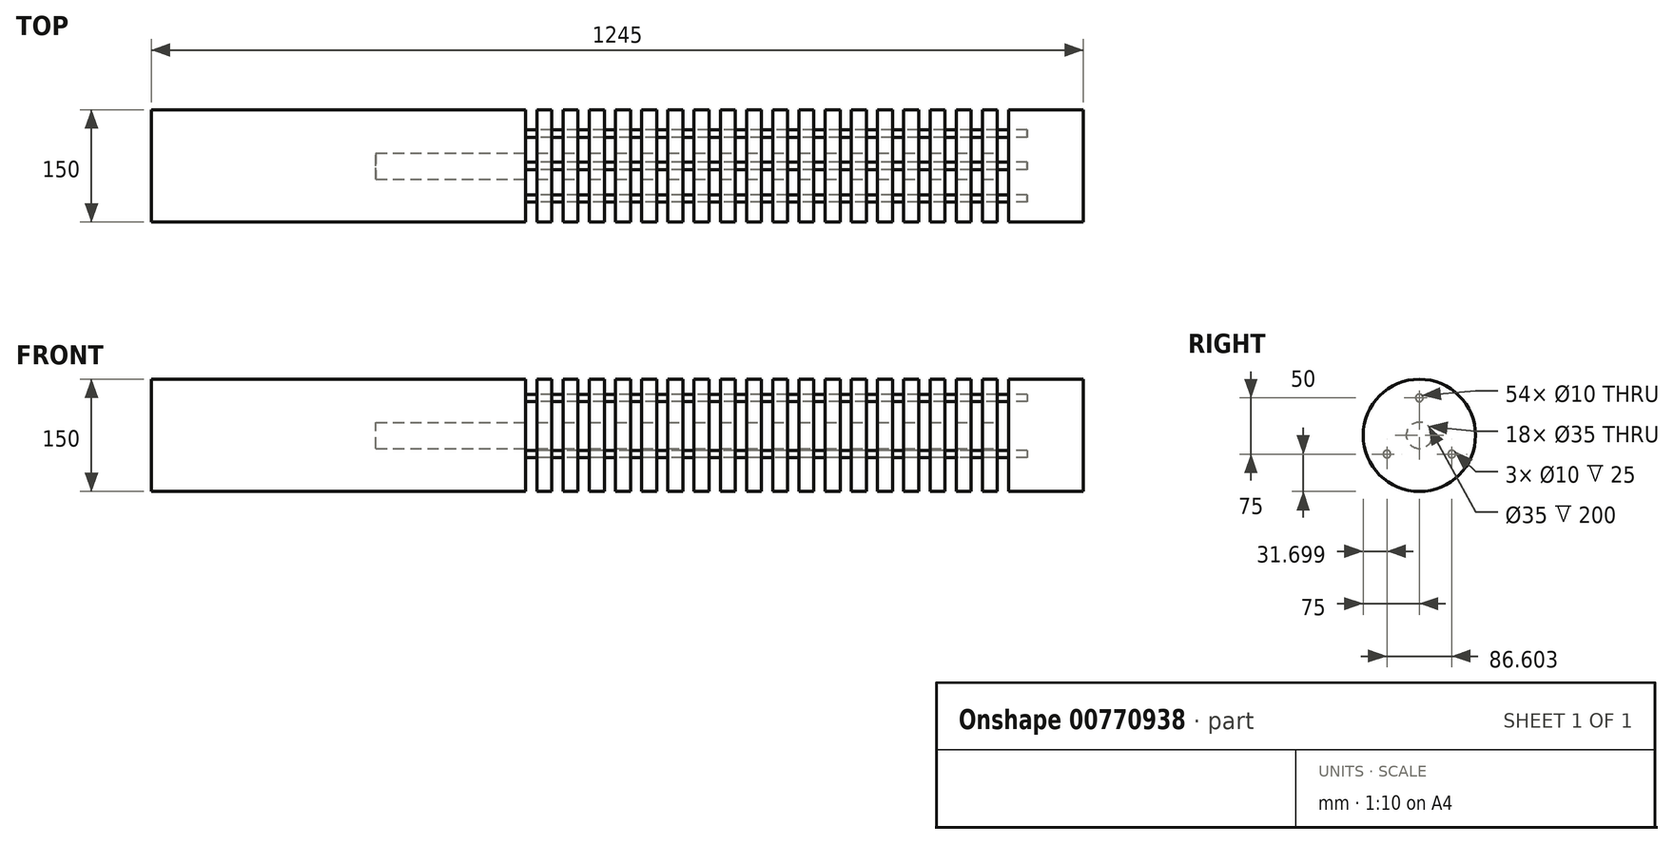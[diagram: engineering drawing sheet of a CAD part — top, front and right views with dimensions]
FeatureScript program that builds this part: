
annotation { "Feature Type Name" : "Feature", "Feature Type Description" : "" }
export const myFeature = defineFeature(function(context is Context, id is Id, definition is map)
    precondition{}
    {
        {
            var Q0;
            Q0=qCreatedBy(makeId("Top.planeOp"),FACE);
            var sketch = newSketch(context, id + "F0", { "sketchPlane" : qUnion([Q0])});
            skLineSegment(sketch, "E0", {"start": v(-500, 0) * mm, "end": v(-500, -75) * mm});
            skLineSegment(sketch, "E1", {"start": v(-500, -75) * mm, "end": v(0, -75) * mm});
            skLineSegment(sketch, "E2", {"start": v(0, -75) * mm, "end": v(0, -17.5) * mm});
            skLineSegment(sketch, "E3", {"start": v(0, -17.5) * mm, "end": v(-200, -17.5) * mm});
            skLineSegment(sketch, "E4", {"start": v(-200, -17.5) * mm, "end": v(-200, 0) * mm});
            skLineSegment(sketch, "E5", {"start": v(-200, 0) * mm, "end": v(-500, 0) * mm});
            skSolve(sketch);
        }
        {
            var Q0;
            Q0=qCreatedBy(makeId("Top.planeOp"),FACE);
            var sketch = newSketch(context, id + "F1", { "sketchPlane" : qUnion([Q0])});
            skLineSegment(sketch, "E6.bottom", {"start": v(15, -17.5) * mm, "end": v(35, -17.5) * mm});
            skLineSegment(sketch, "E6.top", {"start": v(15, -75) * mm, "end": v(35, -75) * mm});
            skLineSegment(sketch, "E6.left", {"start": v(15, -17.5) * mm, "end": v(15, -75) * mm});
            skLineSegment(sketch, "E6.right", {"start": v(35, -17.5) * mm, "end": v(35, -75) * mm});
            skLineSegment(sketch, "E7.1.0.0", {"start": v(50, -75) * mm, "end": v(70, -75) * mm});
            skLineSegment(sketch, "E7.1.0.1", {"start": v(70, -17.5) * mm, "end": v(70, -75) * mm});
            skLineSegment(sketch, "E7.1.0.2", {"start": v(50, -17.5) * mm, "end": v(50, -75) * mm});
            skLineSegment(sketch, "E7.1.0.3", {"start": v(50, -17.5) * mm, "end": v(70, -17.5) * mm});
            skLineSegment(sketch, "E7.2.0.0", {"start": v(85, -75) * mm, "end": v(105, -75) * mm});
            skLineSegment(sketch, "E7.2.0.1", {"start": v(105, -17.5) * mm, "end": v(105, -75) * mm});
            skLineSegment(sketch, "E7.2.0.2", {"start": v(85, -17.5) * mm, "end": v(85, -75) * mm});
            skLineSegment(sketch, "E7.2.0.3", {"start": v(85, -17.5) * mm, "end": v(105, -17.5) * mm});
            skLineSegment(sketch, "E7.3.0.0", {"start": v(120, -75) * mm, "end": v(140, -75) * mm});
            skLineSegment(sketch, "E7.3.0.1", {"start": v(140, -17.5) * mm, "end": v(140, -75) * mm});
            skLineSegment(sketch, "E7.3.0.2", {"start": v(120, -17.5) * mm, "end": v(120, -75) * mm});
            skLineSegment(sketch, "E7.3.0.3", {"start": v(120, -17.5) * mm, "end": v(140, -17.5) * mm});
            skLineSegment(sketch, "E7.4.0.0", {"start": v(155, -75) * mm, "end": v(175, -75) * mm});
            skLineSegment(sketch, "E7.4.0.1", {"start": v(175, -17.5) * mm, "end": v(175, -75) * mm});
            skLineSegment(sketch, "E7.4.0.2", {"start": v(155, -17.5) * mm, "end": v(155, -75) * mm});
            skLineSegment(sketch, "E7.4.0.3", {"start": v(155, -17.5) * mm, "end": v(175, -17.5) * mm});
            skLineSegment(sketch, "E7.5.0.0", {"start": v(190, -75) * mm, "end": v(210, -75) * mm});
            skLineSegment(sketch, "E7.5.0.1", {"start": v(210, -17.5) * mm, "end": v(210, -75) * mm});
            skLineSegment(sketch, "E7.5.0.2", {"start": v(190, -17.5) * mm, "end": v(190, -75) * mm});
            skLineSegment(sketch, "E7.5.0.3", {"start": v(190, -17.5) * mm, "end": v(210, -17.5) * mm});
            skLineSegment(sketch, "E7.6.0.0", {"start": v(225, -75) * mm, "end": v(245, -75) * mm});
            skLineSegment(sketch, "E7.6.0.1", {"start": v(245, -17.5) * mm, "end": v(245, -75) * mm});
            skLineSegment(sketch, "E7.6.0.2", {"start": v(225, -17.5) * mm, "end": v(225, -75) * mm});
            skLineSegment(sketch, "E7.6.0.3", {"start": v(225, -17.5) * mm, "end": v(245, -17.5) * mm});
            skLineSegment(sketch, "E7.7.0.0", {"start": v(260, -75) * mm, "end": v(280, -75) * mm});
            skLineSegment(sketch, "E7.7.0.1", {"start": v(280, -17.5) * mm, "end": v(280, -75) * mm});
            skLineSegment(sketch, "E7.7.0.2", {"start": v(260, -17.5) * mm, "end": v(260, -75) * mm});
            skLineSegment(sketch, "E7.7.0.3", {"start": v(260, -17.5) * mm, "end": v(280, -17.5) * mm});
            skLineSegment(sketch, "E7.8.0.0", {"start": v(295, -75) * mm, "end": v(315, -75) * mm});
            skLineSegment(sketch, "E7.8.0.1", {"start": v(315, -17.5) * mm, "end": v(315, -75) * mm});
            skLineSegment(sketch, "E7.8.0.2", {"start": v(295, -17.5) * mm, "end": v(295, -75) * mm});
            skLineSegment(sketch, "E7.8.0.3", {"start": v(295, -17.5) * mm, "end": v(315, -17.5) * mm});
            skLineSegment(sketch, "E7.9.0.0", {"start": v(330, -75) * mm, "end": v(350, -75) * mm});
            skLineSegment(sketch, "E7.9.0.1", {"start": v(350, -17.5) * mm, "end": v(350, -75) * mm});
            skLineSegment(sketch, "E7.9.0.2", {"start": v(330, -17.5) * mm, "end": v(330, -75) * mm});
            skLineSegment(sketch, "E7.9.0.3", {"start": v(330, -17.5) * mm, "end": v(350, -17.5) * mm});
            skLineSegment(sketch, "E7.10.0.0", {"start": v(365, -75) * mm, "end": v(385, -75) * mm});
            skLineSegment(sketch, "E7.10.0.1", {"start": v(385, -17.5) * mm, "end": v(385, -75) * mm});
            skLineSegment(sketch, "E7.10.0.2", {"start": v(365, -17.5) * mm, "end": v(365, -75) * mm});
            skLineSegment(sketch, "E7.10.0.3", {"start": v(365, -17.5) * mm, "end": v(385, -17.5) * mm});
            skLineSegment(sketch, "E7.11.0.0", {"start": v(400, -75) * mm, "end": v(420, -75) * mm});
            skLineSegment(sketch, "E7.11.0.1", {"start": v(420, -17.5) * mm, "end": v(420, -75) * mm});
            skLineSegment(sketch, "E7.11.0.2", {"start": v(400, -17.5) * mm, "end": v(400, -75) * mm});
            skLineSegment(sketch, "E7.11.0.3", {"start": v(400, -17.5) * mm, "end": v(420, -17.5) * mm});
            skLineSegment(sketch, "E7.12.0.0", {"start": v(435, -75) * mm, "end": v(455, -75) * mm});
            skLineSegment(sketch, "E7.12.0.1", {"start": v(455, -17.5) * mm, "end": v(455, -75) * mm});
            skLineSegment(sketch, "E7.12.0.2", {"start": v(435, -17.5) * mm, "end": v(435, -75) * mm});
            skLineSegment(sketch, "E7.12.0.3", {"start": v(435, -17.5) * mm, "end": v(455, -17.5) * mm});
            skLineSegment(sketch, "E7.13.0.0", {"start": v(470, -75) * mm, "end": v(490, -75) * mm});
            skLineSegment(sketch, "E7.13.0.1", {"start": v(490, -17.5) * mm, "end": v(490, -75) * mm});
            skLineSegment(sketch, "E7.13.0.2", {"start": v(470, -17.5) * mm, "end": v(470, -75) * mm});
            skLineSegment(sketch, "E7.13.0.3", {"start": v(470, -17.5) * mm, "end": v(490, -17.5) * mm});
            skLineSegment(sketch, "E7.14.0.0", {"start": v(505, -75) * mm, "end": v(525, -75) * mm});
            skLineSegment(sketch, "E7.14.0.1", {"start": v(525, -17.5) * mm, "end": v(525, -75) * mm});
            skLineSegment(sketch, "E7.14.0.2", {"start": v(505, -17.5) * mm, "end": v(505, -75) * mm});
            skLineSegment(sketch, "E7.14.0.3", {"start": v(505, -17.5) * mm, "end": v(525, -17.5) * mm});
            skLineSegment(sketch, "E7.15.0.0", {"start": v(540, -75) * mm, "end": v(560, -75) * mm});
            skLineSegment(sketch, "E7.15.0.1", {"start": v(560, -17.5) * mm, "end": v(560, -75) * mm});
            skLineSegment(sketch, "E7.15.0.2", {"start": v(540, -17.5) * mm, "end": v(540, -75) * mm});
            skLineSegment(sketch, "E7.15.0.3", {"start": v(540, -17.5) * mm, "end": v(560, -17.5) * mm});
            skLineSegment(sketch, "E7.16.0.0", {"start": v(575, -75) * mm, "end": v(595, -75) * mm});
            skLineSegment(sketch, "E7.16.0.1", {"start": v(595, -17.5) * mm, "end": v(595, -75) * mm});
            skLineSegment(sketch, "E7.16.0.2", {"start": v(575, -17.5) * mm, "end": v(575, -75) * mm});
            skLineSegment(sketch, "E7.16.0.3", {"start": v(575, -17.5) * mm, "end": v(595, -17.5) * mm});
            skLineSegment(sketch, "E7.17.0.0", {"start": v(610, -75) * mm, "end": v(630, -75) * mm});
            skLineSegment(sketch, "E7.17.0.1", {"start": v(630, -17.5) * mm, "end": v(630, -75) * mm});
            skLineSegment(sketch, "E7.17.0.2", {"start": v(610, -17.5) * mm, "end": v(610, -75) * mm});
            skLineSegment(sketch, "E7.17.0.3", {"start": v(610, -17.5) * mm, "end": v(630, -17.5) * mm});
            skLineSegment(sketch, "E7.direction1", {"start": v(15, -75) * mm, "end": v(50, -75) * mm, "construction": true});
            skSolve(sketch);
        }
        {
            var Q0;
            Q0=qCreatedBy(makeId("Top.planeOp"),FACE);
            var sketch = newSketch(context, id + "F2", { "sketchPlane" : qUnion([Q0])});
            skLineSegment(sketch, "E8.bottom", {"start": v(645, -75) * mm, "end": v(745, -75) * mm});
            skLineSegment(sketch, "E8.top", {"start": v(645, 0) * mm, "end": v(745, 0) * mm});
            skLineSegment(sketch, "E8.left", {"start": v(645, -75) * mm, "end": v(645, 0) * mm});
            skLineSegment(sketch, "E8.right", {"start": v(745, -75) * mm, "end": v(745, 0) * mm});
            skSolve(sketch);
        }
        {
            var Q0;
            Q0=makeQuery(id+"F0.imprint","IMPRINT",FACE,{"disambiguationData":[TD([[makeQuery(id+"F0.imprint","IMPRINT",EDGE,{"derivedFrom":sQuery(id+"F0.wireOp",EDGE,"E0")}),1.0]])]});
            var Q1;
            Q1=makeQuery(id+"F1.imprint","IMPRINT",FACE,{"disambiguationData":[TD([[makeQuery(id+"F1.imprint","IMPRINT",EDGE,{"derivedFrom":sQuery(id+"F1.wireOp",EDGE,"E7.4.0.0")}),1.0]])]});
            var Q2;
            Q2=makeQuery(id+"F1.imprint","IMPRINT",FACE,{"disambiguationData":[TD([[makeQuery(id+"F1.imprint","IMPRINT",EDGE,{"derivedFrom":sQuery(id+"F1.wireOp",EDGE,"E7.9.0.0")}),1.0]])]});
            var Q3;
            Q3=makeQuery(id+"F1.imprint","IMPRINT",FACE,{"disambiguationData":[TD([[makeQuery(id+"F1.imprint","IMPRINT",EDGE,{"derivedFrom":sQuery(id+"F1.wireOp",EDGE,"E7.3.0.0")}),1.0]])]});
            var Q4;
            Q4=makeQuery(id+"F1.imprint","IMPRINT",FACE,{"disambiguationData":[TD([[makeQuery(id+"F1.imprint","IMPRINT",EDGE,{"derivedFrom":sQuery(id+"F1.wireOp",EDGE,"E7.2.0.0")}),1.0]])]});
            var Q5;
            Q5=makeQuery(id+"F1.imprint","IMPRINT",FACE,{"disambiguationData":[TD([[makeQuery(id+"F1.imprint","IMPRINT",EDGE,{"derivedFrom":sQuery(id+"F1.wireOp",EDGE,"E7.10.0.0")}),1.0]])]});
            var Q6;
            Q6=makeQuery(id+"F1.imprint","IMPRINT",FACE,{"disambiguationData":[TD([[makeQuery(id+"F1.imprint","IMPRINT",EDGE,{"derivedFrom":sQuery(id+"F1.wireOp",EDGE,"E7.1.0.0")}),1.0]])]});
            var Q7;
            Q7=makeQuery(id+"F1.imprint","IMPRINT",FACE,{"disambiguationData":[TD([[makeQuery(id+"F1.imprint","IMPRINT",EDGE,{"derivedFrom":sQuery(id+"F1.wireOp",EDGE,"E7.8.0.0")}),1.0]])]});
            var Q8;
            Q8=makeQuery(id+"F1.imprint","IMPRINT",FACE,{"disambiguationData":[TD([[makeQuery(id+"F1.imprint","IMPRINT",EDGE,{"derivedFrom":sQuery(id+"F1.wireOp",EDGE,"E7.17.0.0")}),1.0]])]});
            var Q9;
            Q9=makeQuery(id+"F1.imprint","IMPRINT",FACE,{"disambiguationData":[TD([[makeQuery(id+"F1.imprint","IMPRINT",EDGE,{"derivedFrom":sQuery(id+"F1.wireOp",EDGE,"E7.16.0.0")}),1.0]])]});
            var Q10;
            Q10=makeQuery(id+"F1.imprint","IMPRINT",FACE,{"disambiguationData":[TD([[makeQuery(id+"F1.imprint","IMPRINT",EDGE,{"derivedFrom":sQuery(id+"F1.wireOp",EDGE,"E7.12.0.0")}),1.0]])]});
            var Q11;
            Q11=makeQuery(id+"F1.imprint","IMPRINT",FACE,{"disambiguationData":[TD([[makeQuery(id+"F1.imprint","IMPRINT",EDGE,{"derivedFrom":sQuery(id+"F1.wireOp",EDGE,"E7.5.0.0")}),1.0]])]});
            var Q12;
            Q12=makeQuery(id+"F1.imprint","IMPRINT",FACE,{"disambiguationData":[TD([[makeQuery(id+"F1.imprint","IMPRINT",EDGE,{"derivedFrom":sQuery(id+"F1.wireOp",EDGE,"E7.6.0.0")}),1.0]])]});
            var Q13;
            Q13=makeQuery(id+"F1.imprint","IMPRINT",FACE,{"disambiguationData":[TD([[makeQuery(id+"F1.imprint","IMPRINT",EDGE,{"derivedFrom":sQuery(id+"F1.wireOp",EDGE,"E7.11.0.0")}),1.0]])]});
            var Q14;
            Q14=makeQuery(id+"F1.imprint","IMPRINT",FACE,{"disambiguationData":[TD([[makeQuery(id+"F1.imprint","IMPRINT",EDGE,{"derivedFrom":sQuery(id+"F1.wireOp",EDGE,"E7.7.0.0")}),1.0]])]});
            var Q15;
            Q15=makeQuery(id+"F1.imprint","IMPRINT",FACE,{"disambiguationData":[TD([[makeQuery(id+"F1.imprint","IMPRINT",EDGE,{"derivedFrom":sQuery(id+"F1.wireOp",EDGE,"E6.bottom")}),-1.0]])]});
            var Q16;
            Q16=makeQuery(id+"F1.imprint","IMPRINT",FACE,{"disambiguationData":[TD([[makeQuery(id+"F1.imprint","IMPRINT",EDGE,{"derivedFrom":sQuery(id+"F1.wireOp",EDGE,"E7.14.0.0")}),1.0]])]});
            var Q17;
            Q17=makeQuery(id+"F1.imprint","IMPRINT",FACE,{"disambiguationData":[TD([[makeQuery(id+"F1.imprint","IMPRINT",EDGE,{"derivedFrom":sQuery(id+"F1.wireOp",EDGE,"E7.13.0.0")}),1.0]])]});
            var Q18;
            Q18=makeQuery(id+"F2.imprint","IMPRINT",FACE,{"disambiguationData":[TD([[makeQuery(id+"F2.imprint","IMPRINT",EDGE,{"derivedFrom":sQuery(id+"F2.wireOp",EDGE,"E8.bottom")}),1.0]])]});
            var Q19;
            Q19=makeQuery(id+"F1.imprint","IMPRINT",FACE,{"disambiguationData":[TD([[makeQuery(id+"F1.imprint","IMPRINT",EDGE,{"derivedFrom":sQuery(id+"F1.wireOp",EDGE,"E7.15.0.0")}),1.0]])]});
            var Q20;
            Q20=sQuery(id+"F0.wireOp",EDGE,"E5");
            revolve(context, id + "F3", {"surfaceOperationType" : NewSurfaceOperationType.NEW, "entities" : qUnion([Q0, Q1, Q2, Q3, Q4, Q5, Q6, Q7, Q8, Q9, Q10, Q11, Q12, Q13, Q14, Q15, Q16, Q17, Q18, Q19]), "axis" : qUnion([Q20]), "revolveType" : RevolveType.FULL});
        }
        {
            var Q0;
            Q0=qCreatedBy(makeId("Right.planeOp"),FACE);
            var sketch = newSketch(context, id + "F4", { "sketchPlane" : qUnion([Q0])});
            skCircle(sketch, "E9", {"center": v(0, 50) * mm, "radius": 5 * mm});
            skCircle(sketch, "E10.1.0", {"center": v(-43.3, -25) * mm, "radius": 5 * mm});
            skCircle(sketch, "E10.2.0", {"center": v(43.3, -25) * mm, "radius": 5 * mm});
            skPoint(sketch, "E10.center", {"position": v(0, 0) * mm});
            skSolve(sketch);
        }
        {
            var Q0;
            Q0 = qSketchRegion(id + "F4", true);
            var Q1;
            Q1=makeQuery(id+"F3.opRevolve","SWEPT_FACE",FACE,{"disambiguationData":[OSD([sQuery(id+"F2.wireOp",EDGE,"E8.left")])]});
            extrude(context, id + "F5", {"entities" : qUnion([Q0]), "operationType" : NewBodyOperationType.REMOVE, "endBound" : BoundingType.UP_TO_SURFACE, "depth" : 25 * mm, "endBoundEntityFace" : qUnion([Q1]), "hasOffset" : true, "offsetDistance" : 25 * mm, "offsetOppositeDirection" : true});
        }
        {
            var Q0;
            Q0 = qSketchRegion(id + "F4", true);
            var Q1;
            Q1=makeQuery(id+"F3.opRevolve","SWEPT_FACE",FACE,{"disambiguationData":[OSD([sQuery(id+"F2.wireOp",EDGE,"E8.left")])]});
            extrude(context, id + "F6", {"entities" : qUnion([Q0]), "endBound" : BoundingType.UP_TO_SURFACE, "depth" : 25 * mm, "endBoundEntityFace" : qUnion([Q1]), "hasOffset" : true, "offsetDistance" : 25 * mm, "offsetOppositeDirection" : true});
        }
    });
